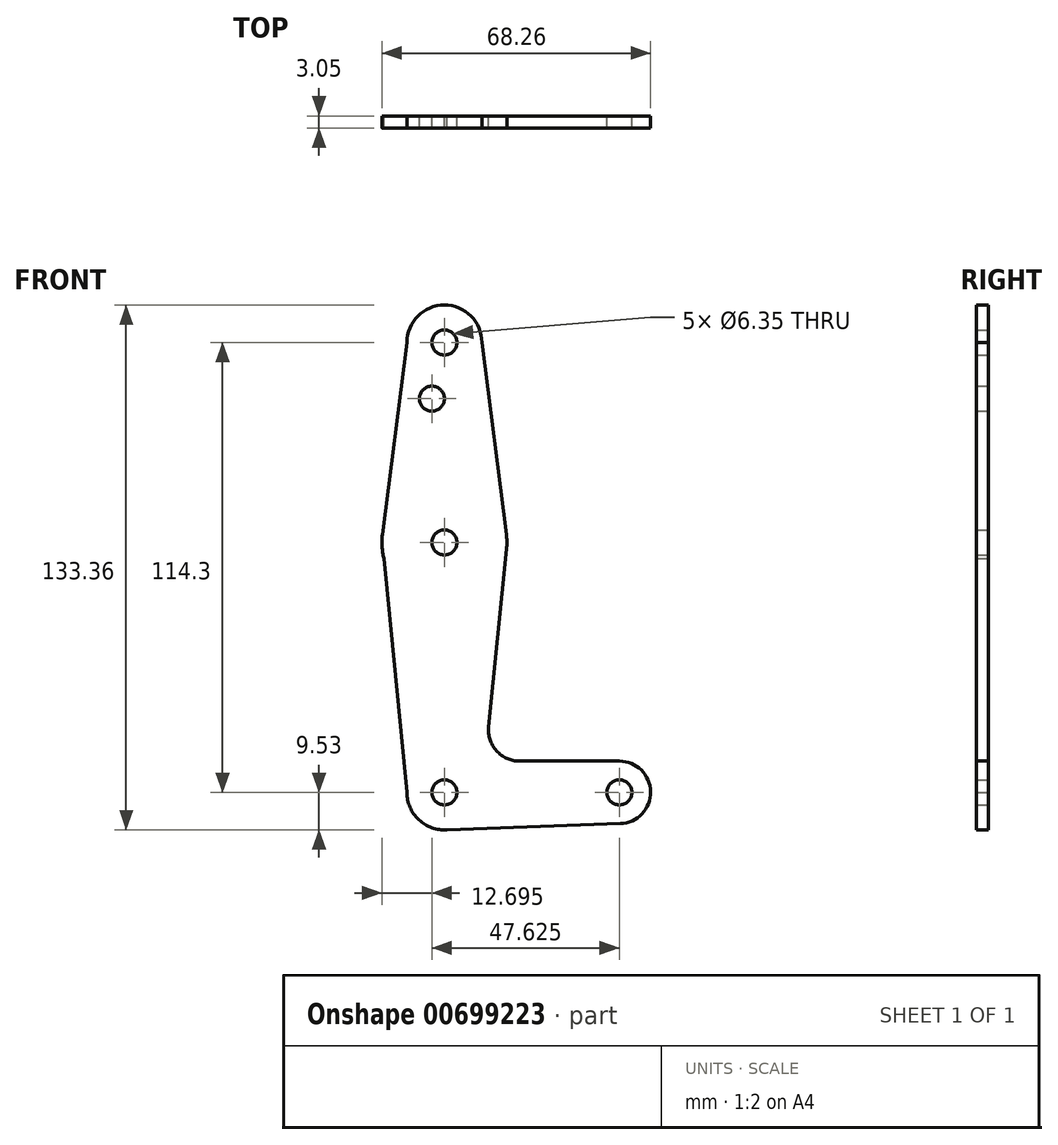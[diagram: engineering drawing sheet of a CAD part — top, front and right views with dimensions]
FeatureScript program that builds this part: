
annotation { "Feature Type Name" : "Feature", "Feature Type Description" : "" }
export const myFeature = defineFeature(function(context is Context, id is Id, definition is map)
    precondition{}
    {
        {
            var Q0;
            Q0=qCreatedBy(makeId("Front.planeOp"),FACE);
            var sketch = newSketch(context, id + "F0", { "sketchPlane" : qUnion([Q0])});
            skLineSegment(sketch, "E0", {"start": v(0, 0) * mm, "end": v(0, 63.5) * mm, "construction": true});
            skLineSegment(sketch, "E1", {"start": v(0, 63.5) * mm, "end": v(0, 114.3) * mm, "construction": true});
            skLineSegment(sketch, "E2", {"start": v(0, 0) * mm, "end": v(44.45, 0) * mm, "construction": true});
            skCircle(sketch, "E3", {"center": v(0, 63.5) * mm, "radius": 15.88 * mm});
            skCircle(sketch, "E4", {"center": v(0, 114.3) * mm, "radius": 9.53 * mm});
            skCircle(sketch, "E5", {"center": v(0, 0) * mm, "radius": 9.53 * mm});
            skCircle(sketch, "E6", {"center": v(44.45, 0) * mm, "radius": 1.27 * mm});
            skCircle(sketch, "E7", {"center": v(44.45, 0) * mm, "radius": 7.94 * mm});
            skLineSegment(sketch, "E8", {"start": v(9.52, 114.3) * mm, "end": v(15.75, 65.5) * mm});
            skLineSegment(sketch, "E9", {"start": v(0, -9.53) * mm, "end": v(44.73, -7.93) * mm});
            skLineSegment(sketch, "E10", {"start": v(-9.53, 114.3) * mm, "end": v(-15.75, 65.5) * mm});
            skLineSegment(sketch, "E11", {"start": v(19.12, 7.94) * mm, "end": v(44.45, 7.94) * mm});
            skLineSegment(sketch, "E12", {"start": v(-15.75, 63.5) * mm, "end": v(-9.52, 0) * mm});
            skLineSegment(sketch, "E13", {"start": v(15.8, 61.9) * mm, "end": v(11.22, 16.69) * mm});
            skCircle(sketch, "E14", {"center": v(0, 114.3) * mm, "radius": 3.18 * mm});
            skCircle(sketch, "E15", {"center": v(-3.18, 100.03) * mm, "radius": 3.18 * mm});
            skCircle(sketch, "E16", {"center": v(0, 63.5) * mm, "radius": 3.18 * mm});
            skCircle(sketch, "E17", {"center": v(0, 0) * mm, "radius": 3.18 * mm});
            skCircle(sketch, "E18", {"center": v(44.45, 0) * mm, "radius": 3.18 * mm});
            skArc(sketch, "E19.filletArc", {"start": v(11.22, 16.69) * mm, "mid": v(13.23, 10.56) * mm, "end": v(19.12, 7.94) * mm});
            skSolve(sketch);
        }
        {
            var Q0;
            Q0 = qSketchRegion(id + "F0", true);
            extrude(context, id + "F1", {"entities" : qUnion([Q0]), "depth" : 3.05 * mm, "offsetDistance" : 25.4 * mm});
        }
    });
